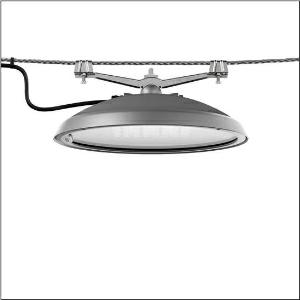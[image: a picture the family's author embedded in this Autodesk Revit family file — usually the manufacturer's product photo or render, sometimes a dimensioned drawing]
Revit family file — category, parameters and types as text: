
# Revit family: dl_r__50_iq_mini___st1_0s_5xa248w31f08he_c7f4
name_source: partatom
category: Lighting Fixtures
units: mm (PartAtom-declared; Revit-internal decimal feet)

## family parameters
Cut with Voids When Loaded = No
Host = Face
Light Source = No
Part Type = Normal
Room Calculation Point = No
Round Connector Dimension = Use Diameter
Shared = No

## types (1)
- --- (1 x LED, 9400 lm, 68.6 W, 3000K)
    Apparent Load = 69 VA
    CIE Flux Codes = 37 72 97 100 100
    Color Rendering = 70
    Color Temperature = 3000K
    Default Elevation = 1800 mm
    Description = DL® 50 iQ mini, catenary luminaire, primary light control with lens, of PMMA, primary optical cover: cover, of toughened safety glass, transparent, light distribution: ST1.0s, light emission: direct distribution, primary light characteristic: symmetric, installation type: suspended mounting, LED, High Power LED, rated luminous flux: 9.400lm, luminous efficacy: 137lm/W, light colour: 730, colour temperature: 3000K, control: optimised constant luminous flux control (CLO 2.0), Desk-Remote (wireless, voltage-free reading and setting of iQ features in the workshop via application-optimized NFC function/RFID function), Light-Fading, Smart-Wire, Night-Set, Lumen-Switch, Temp-Guard, Auto-Match, Street-Remote, mains connection: 230..240V, AC, 50/60Hz, start of lifetime: 69W, end of service life: 72W, reduction: 30W, luminaire housing, of diecast aluminium, powder-coated, Siteco® metallic grey (DB 702S), diameter: 500mm, height: 115mm, protection rating (complete): IP66, insulation class (complete): insulation class II (safety insulation), certification: CE, ENEC, VDE, impact resistance: IK08, permissible operating ambient temperature for outdoor applications: -25..+40°C, standard-compliant lighting for roads and squares, packaging unit: 1 piece

Light Distribution: ST1.0s
    Height = 124 mm  [stored 0.406824 ft]
    Lamp = 1 x LED
    Lamp Light Flux = 9400 lm
    Lamp Power = 68.6 W
    Lamp count = 1
    Length = 500 mm
    Luminous efficacy = 137 lm/W
    Manufacturer = Siteco
    ModVariant = No
    Model = 5XA248W31F08HE
    Number of Poles = 1
    OnlyDefault = Yes
    Power Factor = 1
    Product Name = DL® 50 iQ mini | ST1.0s
    Product group = catenary luminaire
    ProductGroupID = 6300
    Protection Class = Protection class II
    Protection Degree = IP 66
    RLX_Detail_Level = 1
    RLX_Emergency_Light_Flux = 0 lm
    RLX_Emergency_Type = 0
    RLX_Emergency_Type_DB = No
    RlxData = <blob elided: 123677 chars, md5=7e5b7187>
    Socket = socket
    Standby Power = 0 W
    System Light Flux = 9400 lm
    System Power = 69 W
    Type Comments = factory setting: luminous flux: 100 % | dim-lin: 254 | 693 mA
    Type Image = l_1242791.jpg
    URL = http://relux.com
    VarID = @adj_090009
    Voltage = 0 V
    Weight = 0.00 kg
    Width = 0 mm  [stored 0 ft]

note: [stored X ft] marks values corroborated as IEEE doubles in the binary element streams (Revit-internal decimal feet)

## geometry (parser evidence)
native form markers: Blend x4, Sweep x13
no freeform markers — native parametric forms only
